# Revit family: zAccess_Door-Recessed-Cendrex-With_Drywall_Bead_Flange-AHU-GYP
name_source: partatom
category: Specialty Equipment
units: mm (PartAtom-declared; Revit-internal decimal feet)

## family parameters
Cut with Voids When Loaded = No
Enable Cutting in Views = No
Host = Face
Maintain Annotation Orientation = No
OmniClass Number = 23.30.10.27.17
OmniClass Title = Access Doors
Part Type = Normal
Room Calculation Point = No
Round Connector Dimension = Use Diameter
Shared = No

## types (5) — shared parameters
Assembly Code = C1030.80
Available Options = http://cendrex.com
Cendrex LEED Ready Program = http://www.cendrex.com
Construction Material = Metal - Cendrex - Stainless Steel
Description = Large opening removable 20 GA access door with drywall bead flange
Finish = Metal - Cendrex - Powder Coated White
Frame Depth = 2 "
Keynote = 08 10 00
Manufacturer = Cendrex
Model = AHU-GYP
URL = http://www.cendrex.com
Version = 1
zero-valued in all types: Default Elevation

## per-type parameters (varying)
| type | GYP_Height | GYP_Width | Height | Height Calc | Weight | Width | Width Calc |
| 30 x 66 | 66 " | 30 " | 66 " | 66 " | 35.00 lb | 30 " | 30 " |
| 36 x 72 | 72 " | 36 " | 72 " | 72 " | 43.10 lb | 36 " | 36 " |
| 48 x 48 | 48 " | 48 " | 48 " | 48 " | 37.90 lb | 48 " | 48 " |
| Custom | 48 " | 48 " | 48 " | 48 " | 0.00 lb | 48 " | 48 " |
| 30 x 72 | 72 " | 30 " | 72 " | 72 " | 37.80 lb | 30 " | 30 " |

## geometry (parser evidence)
native form markers: Sweep x13
no freeform markers — native parametric forms only
